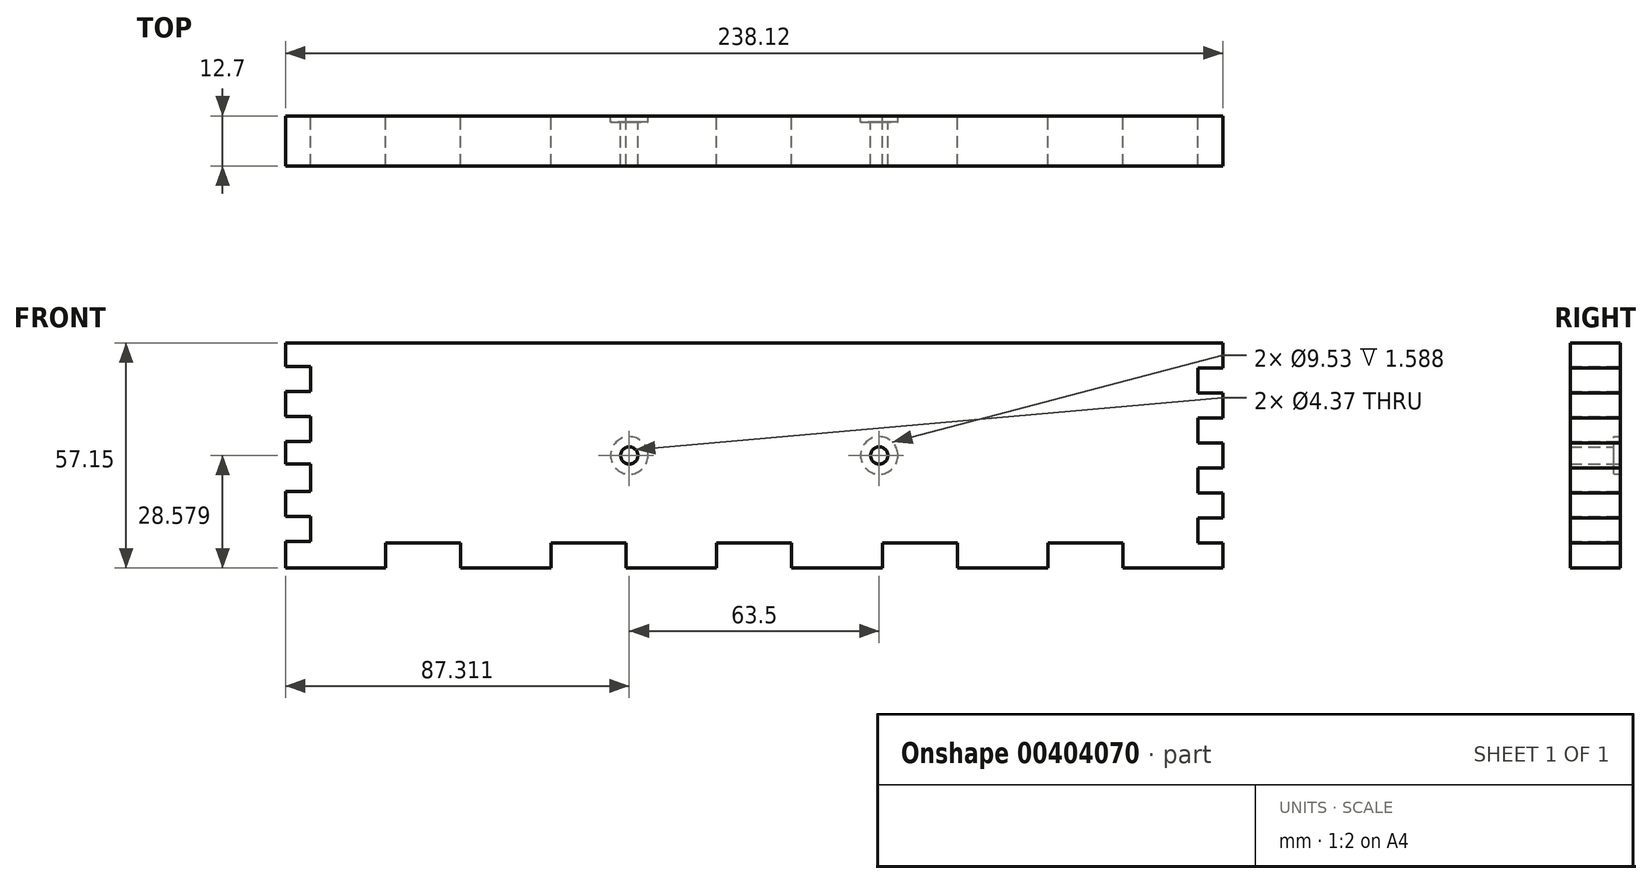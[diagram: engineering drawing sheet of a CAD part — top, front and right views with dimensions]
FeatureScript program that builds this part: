
annotation { "Feature Type Name" : "Feature", "Feature Type Description" : "" }
export const myFeature = defineFeature(function(context is Context, id is Id, definition is map)
    precondition{}
    {
        {
            var Q0;
            Q0=qCreatedBy(makeId("Front.planeOp"),FACE);
            var sketch = newSketch(context, id + "F0", { "sketchPlane" : qUnion([Q0])});
            skLineSegment(sketch, "E0.top", {"start": v(97.37, 34.54) * mm, "end": v(-140.75, 34.54) * mm});
            skLineSegment(sketch, "E0.left", {"start": v(97.37, -22.6) * mm, "end": v(97.37, 34.54) * mm});
            skLineSegment(sketch, "E0.right", {"start": v(-140.75, -22.6) * mm, "end": v(-140.75, 34.54) * mm});
            skPoint(sketch, "E0.middle", {"position": v(-21.69, 5.97) * mm});
            skLineSegment(sketch, "E1.bottom", {"start": v(-12.16, -22.6) * mm, "end": v(-31.21, -22.6) * mm});
            skLineSegment(sketch, "E1.top", {"start": v(-12.16, -16.26) * mm, "end": v(-31.21, -16.26) * mm});
            skLineSegment(sketch, "E1.left", {"start": v(-12.16, -22.6) * mm, "end": v(-12.16, -16.26) * mm});
            skLineSegment(sketch, "E1.right", {"start": v(-31.21, -22.6) * mm, "end": v(-31.21, -16.26) * mm});
            skPoint(sketch, "E1.middle", {"position": v(-21.69, -19.43) * mm});
            skLineSegment(sketch, "E2.bottom", {"start": v(-140.75, -15.95) * mm, "end": v(-134.4, -15.95) * mm});
            skLineSegment(sketch, "E2.top", {"start": v(-140.75, -9.6) * mm, "end": v(-134.4, -9.6) * mm});
            skLineSegment(sketch, "E2.left", {"start": v(-140.75, -15.95) * mm, "end": v(-140.75, -9.6) * mm});
            skLineSegment(sketch, "E2.right", {"start": v(-134.4, -15.95) * mm, "end": v(-134.4, -9.6) * mm});
            skLineSegment(sketch, "E3.0.1.0", {"start": v(-140.75, -3.25) * mm, "end": v(-134.4, -3.25) * mm});
            skLineSegment(sketch, "E3.0.1.1", {"start": v(-134.4, -3.25) * mm, "end": v(-134.4, 3.78) * mm});
            skLineSegment(sketch, "E3.0.1.2", {"start": v(-140.75, 3.78) * mm, "end": v(-134.4, 3.78) * mm});
            skLineSegment(sketch, "E3.0.1.3", {"start": v(-140.75, -3.25) * mm, "end": v(-140.75, 3.78) * mm});
            skLineSegment(sketch, "E3.0.2.0", {"start": v(-140.75, 9.45) * mm, "end": v(-134.4, 9.45) * mm});
            skLineSegment(sketch, "E3.0.2.1", {"start": v(-134.4, 9.45) * mm, "end": v(-134.4, 15.8) * mm});
            skLineSegment(sketch, "E3.0.2.2", {"start": v(-140.75, 15.8) * mm, "end": v(-134.4, 15.8) * mm});
            skLineSegment(sketch, "E3.0.2.3", {"start": v(-140.75, 9.45) * mm, "end": v(-140.75, 15.8) * mm});
            skLineSegment(sketch, "E3.0.3.0", {"start": v(-140.75, 22.15) * mm, "end": v(-134.4, 22.15) * mm});
            skLineSegment(sketch, "E3.0.3.1", {"start": v(-134.4, 22.15) * mm, "end": v(-134.4, 28.5) * mm});
            skLineSegment(sketch, "E3.0.3.2", {"start": v(-140.75, 28.5) * mm, "end": v(-134.4, 28.5) * mm});
            skLineSegment(sketch, "E3.0.3.3", {"start": v(-140.75, 22.15) * mm, "end": v(-140.75, 28.5) * mm});
            skLineSegment(sketch, "E3.direction2", {"start": v(-140.75, -15.95) * mm, "end": v(-140.75, -3.25) * mm, "construction": true});
            skLineSegment(sketch, "E4", {"start": v(-140.75, -22.6) * mm, "end": v(97.37, -22.6) * mm});
            skLineSegment(sketch, "E5.1.0.0", {"start": v(10.85, -22.6) * mm, "end": v(10.85, -16.26) * mm});
            skLineSegment(sketch, "E5.1.0.1", {"start": v(29.9, -22.6) * mm, "end": v(29.9, -16.26) * mm});
            skLineSegment(sketch, "E5.1.0.2", {"start": v(29.9, -16.26) * mm, "end": v(10.85, -16.26) * mm});
            skLineSegment(sketch, "E5.1.0.3", {"start": v(29.9, -22.6) * mm, "end": v(10.85, -22.6) * mm});
            skPoint(sketch, "E5.1.0.4", {"position": v(20.38, -19.43) * mm});
            skLineSegment(sketch, "E5.2.0.0", {"start": v(52.92, -22.6) * mm, "end": v(52.92, -16.26) * mm});
            skLineSegment(sketch, "E5.2.0.1", {"start": v(71.97, -22.6) * mm, "end": v(71.97, -16.26) * mm});
            skLineSegment(sketch, "E5.2.0.2", {"start": v(71.97, -16.26) * mm, "end": v(52.92, -16.26) * mm});
            skLineSegment(sketch, "E5.2.0.3", {"start": v(71.97, -22.6) * mm, "end": v(52.92, -22.6) * mm});
            skPoint(sketch, "E5.2.0.4", {"position": v(62.45, -19.43) * mm});
            skLineSegment(sketch, "E5.direction1", {"start": v(-31.21, -22.6) * mm, "end": v(10.85, -22.6) * mm, "construction": true});
            skLineSegment(sketch, "E6.1.0.0", {"start": v(-54.23, -16.26) * mm, "end": v(-73.28, -16.26) * mm});
            skLineSegment(sketch, "E6.1.0.1", {"start": v(-54.23, -22.6) * mm, "end": v(-54.23, -16.26) * mm});
            skLineSegment(sketch, "E6.1.0.2", {"start": v(-73.28, -22.6) * mm, "end": v(-73.28, -16.26) * mm});
            skPoint(sketch, "E6.1.0.3", {"position": v(-63.76, -19.43) * mm});
            skLineSegment(sketch, "E6.1.0.4", {"start": v(-54.23, -22.6) * mm, "end": v(-73.28, -22.6) * mm});
            skLineSegment(sketch, "E6.2.0.0", {"start": v(-96.3, -16.26) * mm, "end": v(-115.35, -16.26) * mm});
            skLineSegment(sketch, "E6.2.0.1", {"start": v(-96.3, -22.6) * mm, "end": v(-96.3, -16.26) * mm});
            skLineSegment(sketch, "E6.2.0.2", {"start": v(-115.35, -22.6) * mm, "end": v(-115.35, -16.26) * mm});
            skPoint(sketch, "E6.2.0.3", {"position": v(-105.83, -19.43) * mm});
            skLineSegment(sketch, "E6.2.0.4", {"start": v(-96.3, -22.6) * mm, "end": v(-115.35, -22.6) * mm});
            skLineSegment(sketch, "E6.direction1", {"start": v(-31.21, -22.6) * mm, "end": v(-73.28, -22.6) * mm, "construction": true});
            skLineSegment(sketch, "E7.bottom", {"start": v(97.37, 28.2) * mm, "end": v(91.02, 28.2) * mm});
            skLineSegment(sketch, "E7.top", {"start": v(97.37, 21.84) * mm, "end": v(91.02, 21.84) * mm});
            skLineSegment(sketch, "E7.left", {"start": v(97.37, 28.2) * mm, "end": v(97.37, 21.84) * mm});
            skLineSegment(sketch, "E7.right", {"start": v(91.02, 28.2) * mm, "end": v(91.02, 21.84) * mm});
            skLineSegment(sketch, "E8.0.1.0", {"start": v(97.37, 15.5) * mm, "end": v(91.02, 15.5) * mm});
            skLineSegment(sketch, "E8.0.1.1", {"start": v(97.37, 15.5) * mm, "end": v(97.37, 9.14) * mm});
            skLineSegment(sketch, "E8.0.1.2", {"start": v(91.02, 15.5) * mm, "end": v(91.02, 9.14) * mm});
            skLineSegment(sketch, "E8.0.1.3", {"start": v(97.37, 9.14) * mm, "end": v(91.02, 9.14) * mm});
            skLineSegment(sketch, "E8.0.2.0", {"start": v(97.37, 2.8) * mm, "end": v(91.02, 2.8) * mm});
            skLineSegment(sketch, "E8.0.2.1", {"start": v(97.37, 2.8) * mm, "end": v(97.37, -3.56) * mm});
            skLineSegment(sketch, "E8.0.2.2", {"start": v(91.02, 2.8) * mm, "end": v(91.02, -3.56) * mm});
            skLineSegment(sketch, "E8.0.2.3", {"start": v(97.37, -3.56) * mm, "end": v(91.02, -3.56) * mm});
            skLineSegment(sketch, "E8.0.3.0", {"start": v(97.37, -9.9) * mm, "end": v(91.02, -9.9) * mm});
            skLineSegment(sketch, "E8.0.3.1", {"start": v(97.37, -9.9) * mm, "end": v(97.37, -16.26) * mm});
            skLineSegment(sketch, "E8.0.3.2", {"start": v(91.02, -9.9) * mm, "end": v(91.02, -16.26) * mm});
            skLineSegment(sketch, "E8.0.3.3", {"start": v(97.37, -16.26) * mm, "end": v(91.02, -16.26) * mm});
            skCircle(sketch, "E9", {"center": v(-53.44, 5.97) * mm, "radius": 2.18 * mm});
            skCircle(sketch, "E10", {"center": v(10.06, 5.97) * mm, "radius": 2.18 * mm});
            skCircle(sketch, "E11", {"center": v(-53.44, 5.97) * mm, "radius": 4.76 * mm});
            skCircle(sketch, "E12", {"center": v(10.06, 5.97) * mm, "radius": 4.76 * mm});
            skSolve(sketch);
        }
        {
            var Q0;
            Q0=makeQuery(id+"F0.imprint","IMPRINT",FACE,{"disambiguationData":[TD([[makeQuery(id+"F0.imprint","IMPRINT",EDGE,{"derivedFrom":sQuery(id+"F0.wireOp",EDGE,"8OV9EOJX-cDp6-Kej7-olCI-h6javhu7RD7i.bottom")}),-1.0]])]});
            var Q1;
            {var subQ14=sQuery(id+"F0.wireOp",EDGE,"E0.top");Q1=makeQuery(id+"F0.imprint","IMPRINT",FACE,{"disambiguationData":[TD([[makeQuery(id+"F0.imprint","IMPRINT",EDGE,{"derivedFrom":subQ14}),1.0]])]});}
            var Q2;
            Q2=makeQuery(id+"F0.imprint","IMPRINT",FACE,{"disambiguationData":[TD([[makeQuery(id+"F0.imprint","IMPRINT",EDGE,{"derivedFrom":sQuery(id+"F0.wireOp",EDGE,"vm3Zr12K-OBwB-xvDh-h5wd-lU4RoEqm8u74")}),1.0]])]});
            var Q3;
            Q3=makeQuery(id+"F0.imprint","IMPRINT",FACE,{"disambiguationData":[TD([[makeQuery(id+"F0.imprint","IMPRINT",EDGE,{"derivedFrom":sQuery(id+"F0.wireOp",EDGE,"dTZ0A5Tn-MK4k-rhgQ-kAlg-ejJL5lc3IURb")}),1.0]])]});
            extrude(context, id + "F1", {"entities" : qUnion([Q0, Q1, Q2, Q3]), "depth" : 12.7 * mm});
        }
        {
            var Q0;
            Q0=makeQuery(id+"F0.imprint","IMPRINT",FACE,{"disambiguationData":[TD([[makeQuery(id+"F0.imprint","IMPRINT",EDGE,{"derivedFrom":sQuery(id+"F0.wireOp",EDGE,"E9")}),-1.0]])]});
            extrude(context, id + "F2", {"entities" : qUnion([Q0]), "operationType" : NewBodyOperationType.ADD, "depth" : 12.7 * mm, "hasSecondDirection" : true, "secondDirectionOppositeDirection" : true, "secondDirectionDepth" : -1.59 * mm});
        }
        {
            var Q0;
            Q0=makeQuery(id+"F0.imprint","IMPRINT",FACE,{"disambiguationData":[TD([[makeQuery(id+"F0.imprint","IMPRINT",EDGE,{"derivedFrom":sQuery(id+"F0.wireOp",EDGE,"E10")}),-1.0]])]});
            extrude(context, id + "F3", {"entities" : qUnion([Q0]), "operationType" : NewBodyOperationType.ADD, "depth" : 12.7 * mm, "hasSecondDirection" : true, "secondDirectionOppositeDirection" : true, "secondDirectionDepth" : -1.59 * mm});
        }
    });
